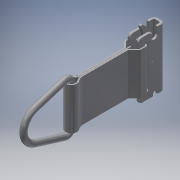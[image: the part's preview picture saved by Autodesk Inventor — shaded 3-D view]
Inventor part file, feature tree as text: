
AUTODESK INVENTOR PART (.ipt)
format: ipt  version: 2018 (Build 220112000, 112)  size: 258,560 bytes
history: native  units: in
note: dims shown in document units (in); Inventor stores cm internally (conversion verified against a paired STEP export)
features: other x3, revolve x1, sweep x1
ambient origin geometry x8: Origin, YZ Plane, XZ Plane, XY Plane, X Axis, Y Axis, Z Axis, Center Point
bodies: Solid1 (feature_tree), Solid2 (feature_tree), Solid3 (feature_tree), Solid4 (feature_tree), Solid5 (feature_tree)
feature tree (5):
  other  "Boss-Extrude2"
  revolve  "Revolve1"  [1 undecoded]
  other  "Boss-Extrude3"
  other  "Boss-Extrude4"
  sweep  "Sweep1"
note: 1 required parameter value undecoded (feature->parameter linkage not recoverable at this tier; creation-order binding heuristic only, values carry confidence <= 0.55)
